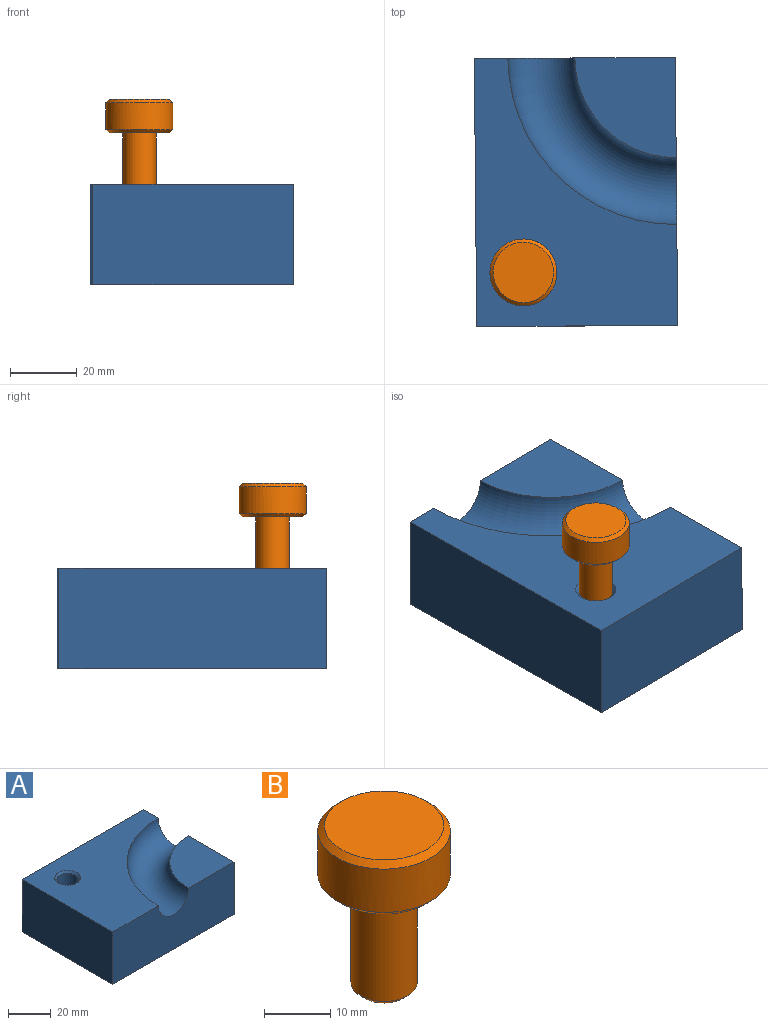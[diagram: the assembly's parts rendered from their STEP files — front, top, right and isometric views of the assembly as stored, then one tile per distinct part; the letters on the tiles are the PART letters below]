
ASSEMBLY  parts=2 mates=1
PART A: 10 faces, bbox 80x60x37.1 mm
  f0: plane 80x60mm, normal (0,0,1), area 2723.4mm2, adj f1,f2,f4,f6,f7,f9
  f1: plane 60x30mm, normal (1,0,0), area 1642.9mm2, adj f0,f2,f3,f5,f6,f7
  f2: plane 80x30mm, normal (0,-1,0), area 2242.9mm2, adj f0,f1,f3,f4,f5,f7
  f3: plane 30x30mm, normal (0,0,1), area 706.9mm2, adj f1,f2,f7
  f4: plane 60x30mm, normal (-1,0,0), area 1800mm2, adj f0,f2,f5,f6
  f5: plane 80x60mm, normal (0,0,-1), area 4721.5mm2, adj f1,f2,f4,f6,f8
  f6: plane 80x30mm, normal (0,1,0), area 2400mm2, adj f0,f1,f4,f5
  f7: torus R=40mm, axis (0,0,-1), area 1973.9mm2, adj f0,f1,f2,f3
  f8: cylinder r=5mm len=29mm, axis (0,0,1), area 911.1mm2, adj f5,f9
  f9: cone r=5mm half-angle=45deg, axis (0,0,1), area 48.9mm2, adj f0,f8
PART B: 8 faces, bbox 20x20x30 mm
  f0: plane 8x8mm, normal (0,0,-1), area 50.3mm2, adj f7
  f1: cylinder r=5mm len=19mm, axis (0,0,1), area 596.9mm2, adj f2,f7
  f2: plane 18x18mm, normal (0,0,-1), area 175.9mm2, adj f1,f5
  f3: cylinder r=10mm len=20mm, axis (0,0,1), area 502.7mm2, adj f5,f6
  f4: plane 18x18mm, normal (0,0,1), area 254.5mm2, adj f6
  f5: cone r=10mm half-angle=45deg, axis (0,0,1), area 84.4mm2, adj f2,f3
  f6: cone r=9mm half-angle=45deg, axis (0,0,-1), area 84.4mm2, adj f3,f4
  f7: cone r=5mm half-angle=45deg, axis (0,0,1), area 40mm2, adj f0,f1
PLACE A rot(axis=(0,0,1),90.5deg) t=(31.69,70.5,1.08)mm fixed
PLACE B rot(axis=(0,0,1),136.2deg) t=(-14.01,46.15,-3.66)mm
MATE cylindrical B.f1 <-> A.f8  axis (0,0,-1) through (-14.01,46.15,-3.66)mm
